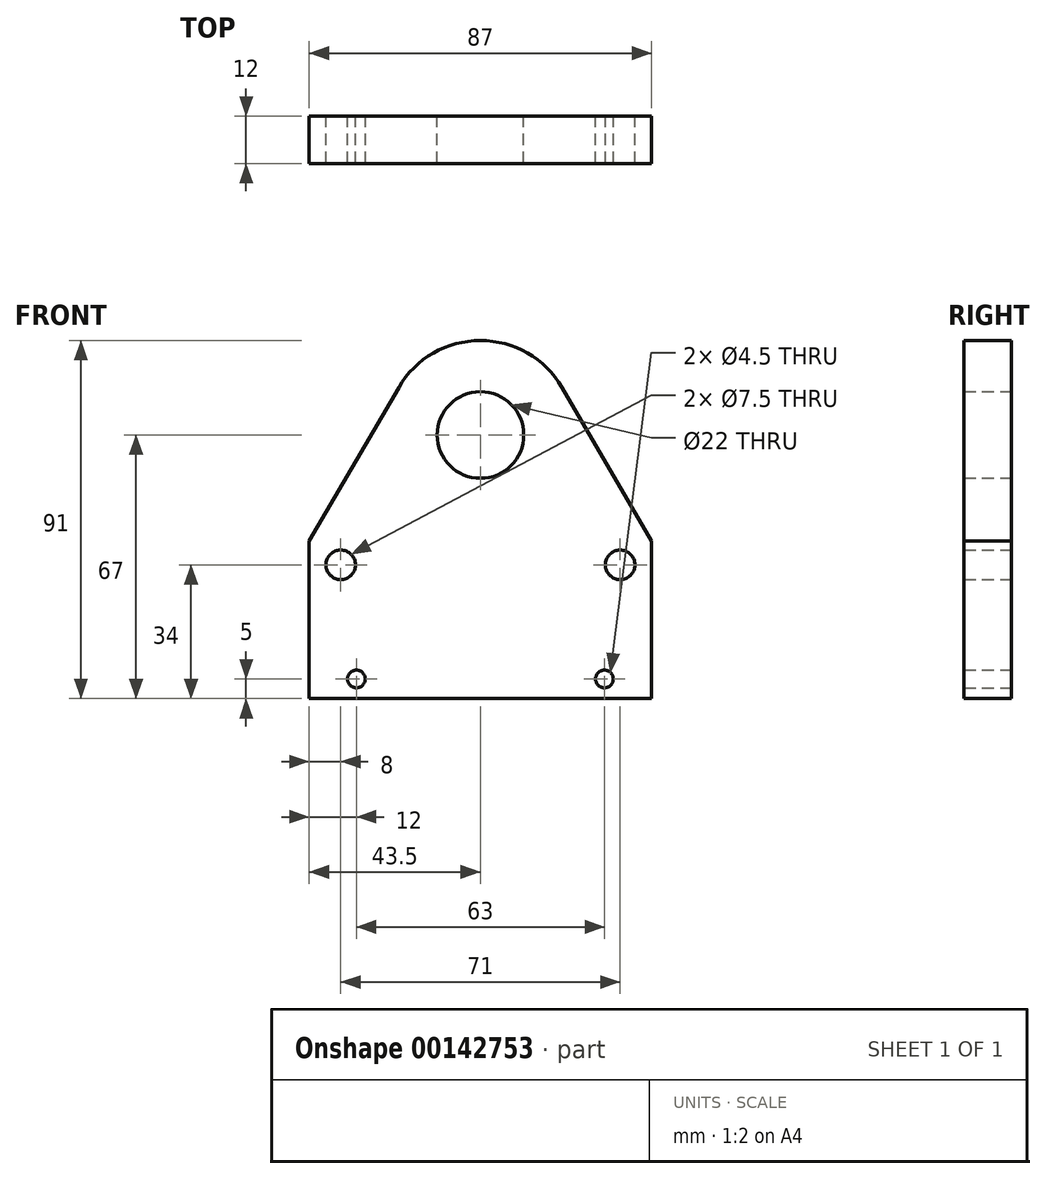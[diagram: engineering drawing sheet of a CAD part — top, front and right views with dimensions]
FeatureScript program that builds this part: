
annotation { "Feature Type Name" : "Feature", "Feature Type Description" : "" }
export const myFeature = defineFeature(function(context is Context, id is Id, definition is map)
    precondition{}
    {
        {
            var Q0;
            Q0=qCreatedBy(makeId("Front.planeOp"),FACE);
            var sketch = newSketch(context, id + "F0", { "sketchPlane" : qUnion([Q0])});
            skLineSegment(sketch, "E0", {"start": v(0, 0) * mm, "end": v(87, 0) * mm});
            skLineSegment(sketch, "E1", {"start": v(87, 0) * mm, "end": v(87, 40) * mm});
            skLineSegment(sketch, "E2", {"start": v(0, 0) * mm, "end": v(0, 40) * mm});
            skCircle(sketch, "E3", {"center": v(43.5, 67) * mm, "radius": 11 * mm});
            skPoint(sketch, "E3.centerSnap0", {"position": v(43.5, 0) * mm});
            skArc(sketch, "E4", {"start": v(64.24, 79.08) * mm, "mid": v(43.5, 91) * mm, "end": v(22.76, 79.08) * mm});
            skCircle(sketch, "E5", {"center": v(8, 34) * mm, "radius": 3.75 * mm});
            skCircle(sketch, "E6", {"center": v(79, 34) * mm, "radius": 3.75 * mm});
            skCircle(sketch, "E7", {"center": v(12, 5) * mm, "radius": 2.25 * mm});
            skCircle(sketch, "E8", {"center": v(75, 5) * mm, "radius": 2.25 * mm});
            skLineSegment(sketch, "E9", {"start": v(0, 40) * mm, "end": v(22.76, 79.08) * mm});
            skLineSegment(sketch, "E10", {"start": v(43.5, 0) * mm, "end": v(43.5, 39.96) * mm, "construction": true});
            skLineSegment(sketch, "E11.MirrorCS", {"start": v(87, 40) * mm, "end": v(64.24, 79.08) * mm});
            skSolve(sketch);
        }
        {
            var Q0;
            Q0=makeQuery(id+"F0.imprint","IMPRINT",FACE,{"disambiguationData":[TD([[makeQuery(id+"F0.imprint","IMPRINT",EDGE,{"derivedFrom":sQuery(id+"F0.wireOp",EDGE,"E0")}),1.0]])]});
            extrude(context, id + "F1", {"entities" : qUnion([Q0]), "depth" : 12 * mm});
        }
    });
